# Revit family: QF_Dietatec_GENIER-475-CH5-FL
name_source: partatom
category: Specialty Equipment
revit_build: Autodesk Revit 2016 (Build: 20150220_1215(x64)
units: mm (PartAtom-declared; Revit-internal decimal feet)

## family parameters
Always vertical = Yes
Cut with Voids When Loaded = No
OmniClass Number = 23.40.40.14
OmniClass Title = Food Service Equipment
Part Type = Normal
Room Calculation Point = No
Round Connector Dimension = Use Diameter
Shared = No
Work Plane-Based = No

## types (1)
- 58020-50354
    Accessory = No
    Apparent Power = 51000 VA
    Assembly Code = E1090320
    Cold Water Flow = 0.0 L/s
    Cold Water Size = 13 mm
    Cold Water Temperature Recommended = 0 °C
    Conn Conduit = No
    Cost = 0 $
    Cycle = 50 Hz
    Depth Actual = 1335 mm  [stored 4.37992 ft]
    Description = GENIER ACE CIRCULATED CHILLING MIXER KETTLE WITH INTEGRATED RETURN PUMP, 475L
    Electric power = 51000 W
    FL Amps = 74 A
    Height Actual = 1331 mm
    Length Actual = 1630 mm
    Manufacturer = DIETATEC
    Max Overcurrent Protection = 0 A
    Min Ckt Ampacity = 0 A
    Model = GENIER ACE 475 CH5 FL
    Number of Poles = 3
    Phase = 3
    URL = www.dietatec.com
    Volts = 400 V
    Weight = 545.00 kg

note: [stored X ft] marks values corroborated as IEEE doubles in the binary element streams (Revit-internal decimal feet)

## geometry (parser evidence)
native form markers: Sweep x4
no freeform markers — native parametric forms only
